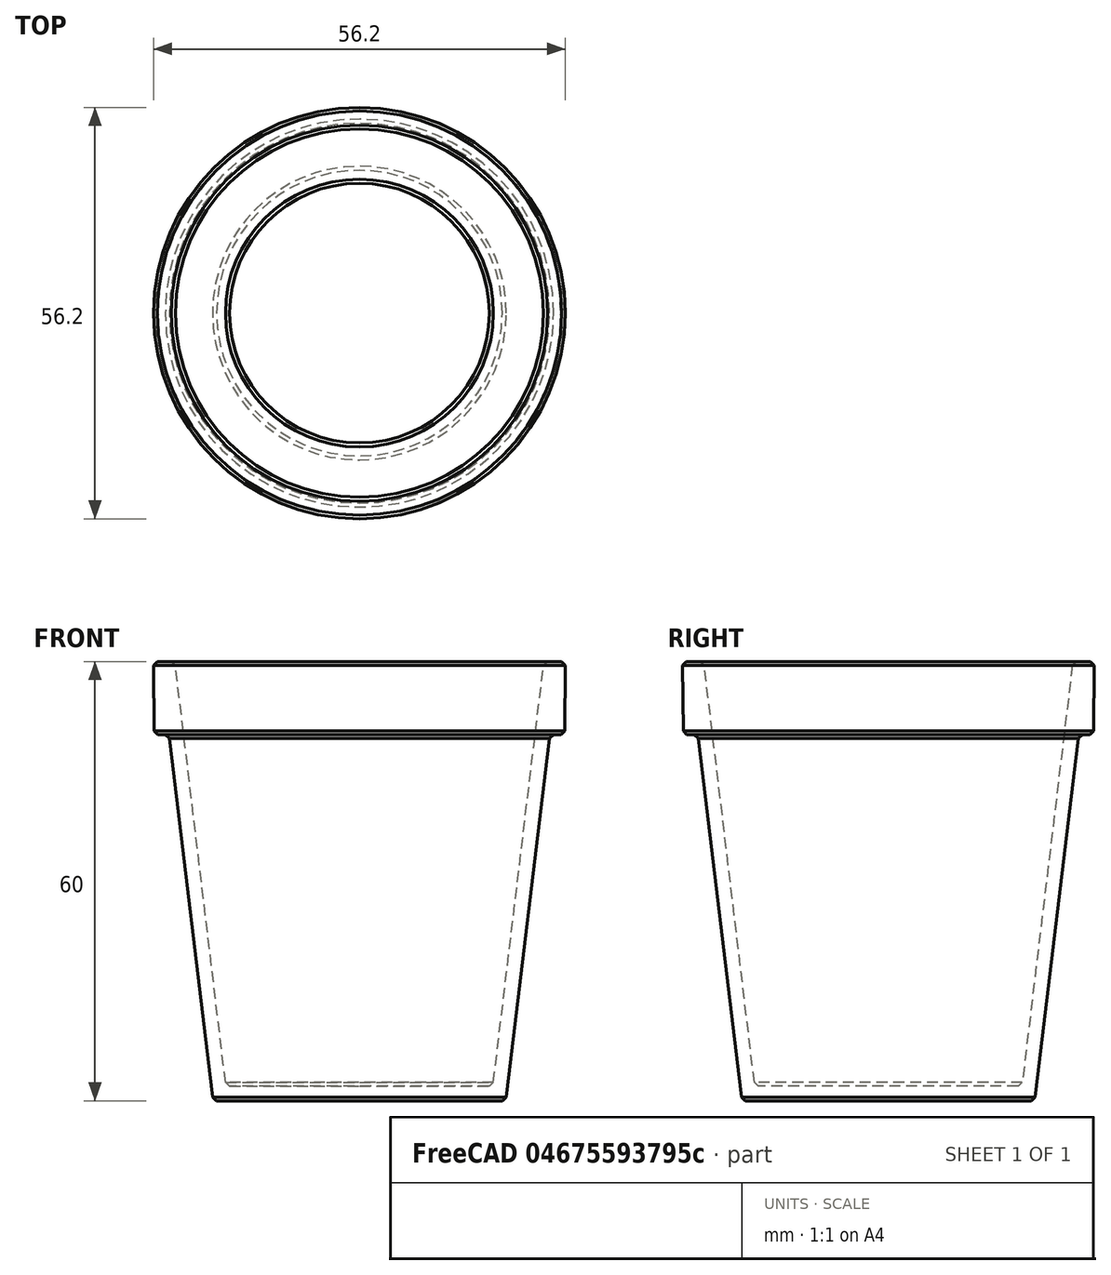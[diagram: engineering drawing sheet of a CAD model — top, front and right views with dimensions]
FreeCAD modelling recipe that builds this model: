
FCSTD DOCUMENT  (FreeCAD 0.19R24291 (Git))
Label: pot 20-60
License: All rights reserved
LicenseURL: http://en.wikipedia.org/wiki/All_rights_reserved
objects: TechDraw::DrawViewDimension×10, TechDraw::DrawProjGroupItem×2, Spreadsheet::Sheet×1, TechDraw::DrawSVGTemplate×1, Sketcher::SketchObject×1, PartDesign::Revolution×1, PartDesign::Chamfer×1, PartDesign::Body×1, TechDraw::DrawProjGroup×1, TechDraw::DrawViewSection×1, TechDraw::DrawPage×1
note: 6 computed .brp shape members not serialized (recipe doc carries the construction recipe); baked Part::Feature solids carry a one-line shape summary decoded from their .brp

FEATURE [Spreadsheet::Sheet] Spreadsheet  label="data"
  cells = A2=rayon_inf_exterieur; B2=20; A3=hauteur_exterieur; B3=60; A4=epaisseur; B4=2; A5=hauteur_rebord; B5=10; A6=rayon_exterieur_total; B6=28
FEATURE [TechDraw::DrawSVGTemplate] Template
  EditableTexts = Designed_by_Name=Designed by <owner>; Drawing_number=46300-1; FC-Date=15 sept 2021; FC-SC=1:1; FC-SH=1/1; FC-Title=Mini Pot de fleur; Subtitle=Pour injection; Weight=Indefini
  Height = 210
  Orientation = 1
  Width = 297
FEATURE [Sketcher::SketchObject] Sketch
  FullyConstrained = true
  MapMode = 5
  Placement = pos=(0,0,0) rot=(0.57735,0.57735,0.57735;2.0944rad)
  Support = -> [YZ_Plane]
  expr: Constraints[20] = <<data>>.B2
  expr: Constraints[19] = <<data>>.B3
  expr: Constraints[21] = <<data>>.B4
  expr: Constraints[14] = <<data>>.B4
  expr: Constraints[17] = <<data>>.B5
  expr: Constraints[22] = <<data>>.B6
  expr: Constraints[16] = <<data>>.B4
  sketch-geometry (8):
    g0: LineSegment StartX=0 StartY=0 StartZ=0 EndX=20 EndY=0 EndZ=0
    g1: LineSegment StartX=20 StartY=0 StartZ=0 EndX=26 EndY=50 EndZ=0
    g2: LineSegment StartX=26 StartY=50 StartZ=0 EndX=28 EndY=50 EndZ=0
    g3: LineSegment StartX=28 StartY=50 StartZ=0 EndX=28.1 EndY=60 EndZ=0
    g4: LineSegment StartX=28.1 StartY=60 StartZ=0 EndX=25.1857 EndY=60 EndZ=0
    g5: LineSegment StartX=25.1857 StartY=60 StartZ=0 EndX=18.2257 EndY=2 EndZ=0
    g6: LineSegment StartX=18.2257 StartY=2 StartZ=0 EndX=0 EndY=2 EndZ=0
    g7: LineSegment StartX=0 StartY=2 StartZ=0 EndX=0 EndY=0 EndZ=0
  constraints (23):
    c: Coincident(g-1,g0)
    c: PointOnObject(g0,g-1)
    c: Coincident(g0,g1)
    c: Coincident(g1,g2)
    c: Horizontal(g2)
    c: Coincident(g2,g3)
    c: Coincident(g3,g4)
    c: Horizontal(g4)
    c: Coincident(g4,g5)
    c: Coincident(g5,g6)
    c: PointOnObject(g6,g-2)
    c: Horizontal(g6)
    c: Coincident(g6,g7)
    c: Coincident(g7,g0)
    c: DistanceY(g7,g7) = 2
    c: Parallel(g5,g1)
    c: DistanceX(g2,g2) = 2
    c: DistanceY(g3,g3) = 10
    c: DistanceX(g2,g3) = 0.1
    c: DistanceY(g0,g3) = 60
    c: DistanceX(g0,g0) = 20
    c: Distance(g5,g1) = 2
    c: DistanceX(g0,g2) = 28
FEATURE [PartDesign::Revolution] Revolution
  Angle = 360
  Axis = (-2e-16,3e-16,1)
  Base = (0,0,0)
  Placement = pos=(0,0,0) rot=(0.57735,0.57735,0.57735;2.0944rad)
  Profile = -> Sketch
  ReferenceAxis = -> Sketch [V_Axis]
  Reversed = true
FEATURE [PartDesign::Chamfer] Chamfer
  Angle = 45
  Base = -> Revolution [Edge1,Edge4,Edge2,Edge5,Edge7,Edge8]
  BaseFeature = -> Revolution
  ChamferType = 0
  FlipDirection = false
  Placement = pos=(0,0,0) rot=(0.57735,0.57735,0.57735;2.0944rad)
  Size = 0.5
  Size2 = 1
  SupportTransform = false
FEATURE [PartDesign::Body] Body
  Group = -> [Sketch,Revolution,Chamfer]
  Origin = -> Origin
  Tip = -> Chamfer
FEATURE [TechDraw::DrawProjGroupItem] ProjItem  label="Front"
  CoarseView = false
  Direction = (1,0,0)
  Focus = 100
  HardHidden = false
  IsoCount = 0
  IsoHidden = false
  IsoVisible = false
  LockPosition = true
  Perspective = false
  Rotation = 0
  RotationVector = (0,1,0)
  ScaleType = 2
  SeamHidden = false
  SeamVisible = true
  SmoothHidden = false
  SmoothVisible = true
  Source = -> [Body]
  Type = 0
  X = 0
  XDirection = (0,1,0)
  Y = 0
FEATURE [TechDraw::DrawProjGroupItem] ProjItem003  label="Top"
  CoarseView = false
  Direction = (0,0,1)
  Focus = 100
  HardHidden = false
  IsoCount = 0
  IsoHidden = false
  IsoVisible = false
  LockPosition = false
  Perspective = false
  Rotation = 0
  RotationVector = (1,0,0)
  ScaleType = 2
  SeamHidden = false
  SeamVisible = true
  SmoothHidden = false
  SmoothVisible = true
  Source = -> [Body]
  Type = 4
  X = 0
  XDirection = (0,1,0)
  Y = -76.905
FEATURE [TechDraw::DrawProjGroup] ProjGroup
  Anchor = -> ProjItem
  AutoDistribute = true
  LockPosition = false
  ProjectionType = 0
  Rotation = 0
  ScaleType = 0
  Source = -> [Body]
  Views = -> [ProjItem,ProjItem003]
  X = 62.7238
  Y = 147.057
  spacingX = 15
  spacingY = 15
FEATURE [TechDraw::DrawViewDimension] Dimension001
  Arbitrary = false
  ArbitraryTolerances = false
  EqualTolerance = true
  FormatSpec = %.2f
  FormatSpecOverTolerance = %+.2f
  FormatSpecUnderTolerance = %+.2f
  Inverted = false
  LockPosition = false
  MeasureType = 1
  OverTolerance = 0
  References2D = -> [ProjItem]
  Rotation = 0
  ScaleType = 0
  TheoreticalExact = false
  Type = 2
  UnderTolerance = 0
  X = 33.9957
  Y = -0.712209
FEATURE [TechDraw::DrawViewDimension] Dimension002
  Arbitrary = false
  ArbitraryTolerances = false
  EqualTolerance = true
  FormatSpec = ⌀%.2f
  FormatSpecOverTolerance = %+.2f
  FormatSpecUnderTolerance = %+.2f
  Inverted = false
  LockPosition = false
  MeasureType = 1
  OverTolerance = 0
  References2D = -> [ProjItem003]
  Rotation = 0
  ScaleType = 0
  TheoreticalExact = false
  Type = 5
  UnderTolerance = 0
  X = 35.8478
  Y = 25.8769
FEATURE [TechDraw::DrawViewDimension] Dimension003
  Arbitrary = false
  ArbitraryTolerances = false
  EqualTolerance = true
  FormatSpec = ⌀%.2f
  FormatSpecOverTolerance = %+.2f
  FormatSpecUnderTolerance = %+.2f
  Inverted = false
  LockPosition = false
  MeasureType = 1
  OverTolerance = 0
  References2D = -> [ProjItem003]
  Rotation = 0
  ScaleType = 0
  TheoreticalExact = false
  Type = 5
  UnderTolerance = 0
  X = 38.2219
  Y = -9.49612
FEATURE [TechDraw::DrawViewDimension] Dimension
  Arbitrary = false
  ArbitraryTolerances = false
  EqualTolerance = true
  FormatSpec = %.2f
  FormatSpecOverTolerance = %+.2f
  FormatSpecUnderTolerance = %+.2f
  Inverted = false
  LockPosition = false
  MeasureType = 1
  OverTolerance = 0
  References2D = -> [ProjItem]
  Rotation = 0
  ScaleType = 0
  TheoreticalExact = false
  Type = 1
  UnderTolerance = 0
  X = -0.238517
  Y = -13.7013
FEATURE [TechDraw::DrawViewSection] SectionView  label="Section A - A"
  BaseView = -> ProjItem
  CoarseView = false
  CutSurfaceDisplay = 2
  Direction = (0,1,0)
  FileGeomPattern = C:/Program Files/FreeCAD 0.19/data/Mod/TechDraw/PAT/FCPAT.pat
  FileHatchPattern = C:/Program Files/FreeCAD 0.19/data/Mod/TechDraw/Patterns/simple.svg
  Focus = 100
  FuseBeforeCut = false
  HardHidden = false
  HatchScale = 1
  IsoCount = 0
  IsoHidden = false
  IsoVisible = false
  LockPosition = false
  NameGeomPattern = Diamond
  Perspective = false
  Rotation = 0
  ScaleType = 0
  SeamHidden = false
  SeamVisible = true
  SectionDirection = 1
  SectionNormal = (0,1,0)
  SectionOrigin = (0,0,30)
  SectionSymbol = A
  SmoothHidden = false
  SmoothVisible = true
  Source = -> [Body]
  X = 196.165
  XDirection = (-1,0,0)
  Y = 144.661
FEATURE [TechDraw::DrawViewDimension] Dimension004
  Arbitrary = false
  ArbitraryTolerances = false
  EqualTolerance = true
  FormatSpec = %.2f
  FormatSpecOverTolerance = %+.2f
  FormatSpecUnderTolerance = %+.2f
  Inverted = false
  LockPosition = false
  MeasureType = 1
  OverTolerance = 0
  References2D = -> [SectionView]
  Rotation = 0
  ScaleType = 0
  TheoreticalExact = false
  Type = 1
  UnderTolerance = 0
  X = 1.61286
  Y = -39.5763
FEATURE [TechDraw::DrawViewDimension] Dimension005
  Arbitrary = false
  ArbitraryTolerances = false
  EqualTolerance = true
  FormatSpec = %.2f
  FormatSpecOverTolerance = %+.2f
  FormatSpecUnderTolerance = %+.2f
  Inverted = false
  LockPosition = false
  MeasureType = 1
  OverTolerance = 0
  References2D = -> [SectionView]
  Rotation = 0
  ScaleType = 0
  TheoreticalExact = false
  Type = 2
  UnderTolerance = 0
  X = 39.6667
  Y = 11.2614
FEATURE [TechDraw::DrawViewDimension] Dimension006
  Arbitrary = false
  ArbitraryTolerances = false
  EqualTolerance = true
  FormatSpec = %.2f
  FormatSpecOverTolerance = %+.2f
  FormatSpecUnderTolerance = %+.2f
  Inverted = false
  LockPosition = false
  MeasureType = 1
  OverTolerance = 0
  References2D = -> [SectionView]
  Rotation = 0
  ScaleType = 0
  TheoreticalExact = false
  Type = 2
  UnderTolerance = 0
  X = 56.3669
  Y = 0.286221
FEATURE [TechDraw::DrawViewDimension] Dimension007
  Arbitrary = false
  ArbitraryTolerances = false
  EqualTolerance = true
  FormatSpec = %.2f
  FormatSpecOverTolerance = %+.2f
  FormatSpecUnderTolerance = %+.2f
  Inverted = false
  LockPosition = false
  MeasureType = 1
  OverTolerance = 0
  References2D = -> [SectionView]
  Rotation = 0
  ScaleType = 0
  TheoreticalExact = false
  Type = 1
  UnderTolerance = 0
  X = 2.38517
  Y = 39.9029
FEATURE [TechDraw::DrawViewDimension] Dimension009
  Arbitrary = false
  ArbitraryTolerances = false
  EqualTolerance = true
  FormatSpec = %.2f
  FormatSpecOverTolerance = %+.2f
  FormatSpecUnderTolerance = %+.2f
  Inverted = false
  LockPosition = false
  MeasureType = 1
  OverTolerance = 0
  References2D = -> [SectionView]
  Rotation = 0
  ScaleType = 0
  TheoreticalExact = false
  Type = 1
  UnderTolerance = 0
  X = 48.0647
  Y = 14.817
FEATURE [TechDraw::DrawViewDimension] Dimension008
  Arbitrary = false
  ArbitraryTolerances = false
  EqualTolerance = true
  FormatSpec = %.2f
  FormatSpecOverTolerance = %+.2f
  FormatSpecUnderTolerance = %+.2f
  Inverted = false
  LockPosition = false
  MeasureType = 1
  OverTolerance = 0
  References2D = -> [SectionView]
  Rotation = 0
  ScaleType = 0
  TheoreticalExact = false
  Type = 1
  UnderTolerance = 0
  X = -33.289
  Y = 35.7987
FEATURE [TechDraw::DrawPage] Page
  KeepUpdated = true
  NextBalloonIndex = 2
  ProjectionType = 0
  Template = -> Template
  Views = -> [ProjGroup,Dimension001,Dimension002,Dimension003,Dimension,SectionView,Dimension004,Dimension005,Dimension006,Dimension007,Dimension008,Dimension009]
